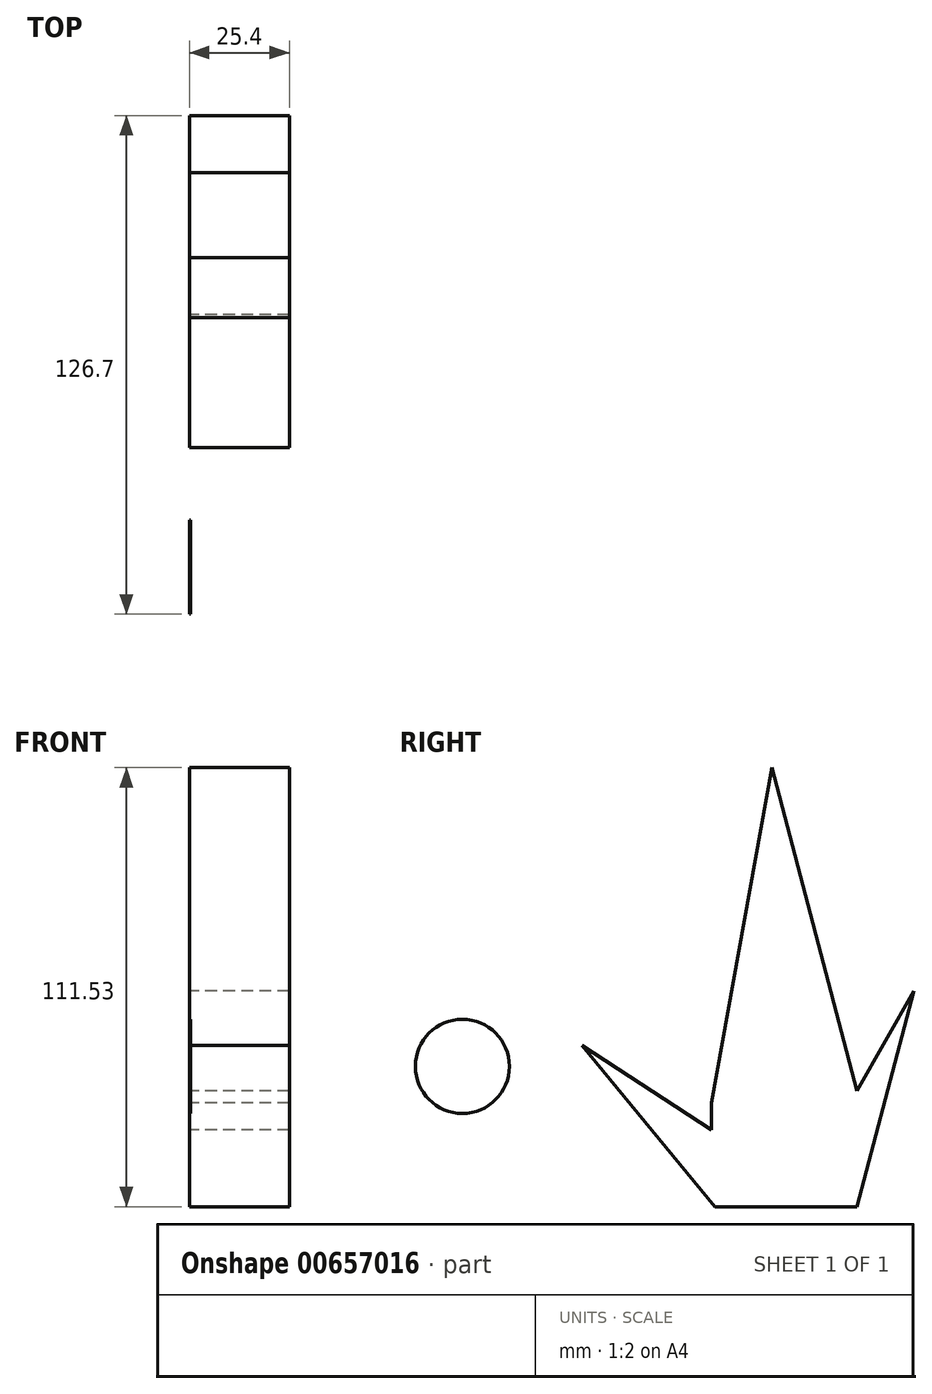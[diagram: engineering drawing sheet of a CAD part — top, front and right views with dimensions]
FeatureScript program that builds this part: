
annotation { "Feature Type Name" : "Feature", "Feature Type Description" : "" }
export const myFeature = defineFeature(function(context is Context, id is Id, definition is map)
    precondition{}
    {
        {
            var Q0;
            Q0=qCreatedBy(makeId("Right.planeOp"),FACE);
            var sketch = newSketch(context, id + "F0", { "sketchPlane" : qUnion([Q0])});
            skCircle(sketch, "E0", {"center": v(-60.5, 38.55) * mm, "radius": 14.09 * mm});
            skSolve(sketch);
        }
        {
            var Q0;
            Q0=makeQuery(id+"F0.imprint","IMPRINT",FACE,{"disambiguationData":[TD([[makeQuery(id+"F0.imprint","IMPRINT",EDGE,{"derivedFrom":sQuery(id+"F0.wireOp",EDGE,"E0")}),1.0]])]});
            extrude(context, id + "F1", {"entities" : qUnion([Q0]), "depth" : 0.25 * mm, "offsetDistance" : 25.4 * mm});
        }
        {
            var Q0;
            Q0=makeQuery(id+"F1.opExtrude","SWEPT_BODY",BODY,{"disambiguationData":[OSD([sQuery(id+"F0.wireOp",EDGE,"E0")])]});
            deleteBodies(context, id + "F2", {"entities" : qUnion([Q0])});
        }
        {
            var Q0;
            Q0=qCreatedBy(makeId("Right.planeOp"),FACE);
            var sketch = newSketch(context, id + "F3", { "sketchPlane" : qUnion([Q0])});
            skCircle(sketch, "E1", {"center": v(-43.15, 35.65) * mm, "radius": 11.95 * mm});
            skSolve(sketch);
        }
        {
            var Q0;
            Q0 = qSketchRegion(id + "F3", true);
            extrude(context, id + "F4", {"entities" : qUnion([Q0]), "depth" : 0.25 * mm, "offsetDistance" : 25.4 * mm});
        }
        {
            var Q0;
            Q0=qCreatedBy(makeId("Right.planeOp"),FACE);
            var sketch = newSketch(context, id + "F5", { "sketchPlane" : qUnion([Q0])});
            skLineSegment(sketch, "E2", {"start": v(20.2, 26.36) * mm, "end": v(35.54, 111.53) * mm});
            skLineSegment(sketch, "E3", {"start": v(35.54, 111.53) * mm, "end": v(57.02, 29.43) * mm});
            skLineSegment(sketch, "E4", {"start": v(57.02, 29.43) * mm, "end": v(71.6, 54.75) * mm});
            skLineSegment(sketch, "E5", {"start": v(71.6, 54.75) * mm, "end": v(57.02, 0) * mm});
            skLineSegment(sketch, "E6", {"start": v(57.02, 0) * mm, "end": v(20.96, 0) * mm});
            skLineSegment(sketch, "E7", {"start": v(20.96, 0) * mm, "end": v(-12.8, 40.94) * mm});
            skLineSegment(sketch, "E8", {"start": v(-12.8, 40.94) * mm, "end": v(20.2, 19.46) * mm});
            skLineSegment(sketch, "E9", {"start": v(20.2, 26.36) * mm, "end": v(20.2, 19.46) * mm});
            skSolve(sketch);
        }
        {
            var Q0;
            Q0 = qSketchRegion(id + "F5", true);
            extrude(context, id + "F6", {"entities" : qUnion([Q0]), "depth" : 25.4 * mm, "offsetDistance" : 25.4 * mm});
        }
    });
